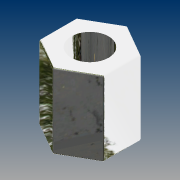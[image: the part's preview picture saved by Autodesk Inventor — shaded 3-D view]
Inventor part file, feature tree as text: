
AUTODESK INVENTOR PART (.ipt)
format: ipt  version: 2015 (Build 190159000, 159)  size: 136,192 bytes
history: native  units: mm
features: extrude x2, fillet x2, sketch x2
ambient origin geometry x8: Origin, YZ Plane, XZ Plane, XY Plane, X Axis, Y Axis, Z Axis, Center Point
bodies: Solid1 (feature_tree)
feature tree (6):
  extrude  "Extrusion1"  Depth=100.0mm
  extrude  "Extrusion2"  TaperAngle=0.0deg  [1 undecoded]
  fillet  "Fillet1"  Radius=100.0mm
  fillet  "Fillet2"  Radius=2.0mm
  sketch  "Sketch1"  dims[d0=100.0mm d1=50.0mm]
  sketch  "Sketch2"  dims[d2=100.0mm d3=0.0mm d4=0.0mm d5=100.0mm d6=0.0mm d7=2.0mm d8=2.0mm]
note: 1 required parameter value undecoded (feature->parameter linkage not recoverable at this tier; creation-order binding heuristic only, values carry confidence <= 0.55)
